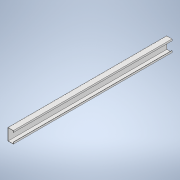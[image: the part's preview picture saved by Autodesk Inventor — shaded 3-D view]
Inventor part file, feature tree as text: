
AUTODESK INVENTOR PART (.ipt)
format: ipt  version: 2020 (Build 240168000, 168)  size: 112,640 bytes
history: native  units: mm
features: extrude x1, sketch x1
ambient origin geometry x8: Origin, YZ Plane, XZ Plane, XY Plane, X Axis, Y Axis, Z Axis, Center Point
bodies: Solid1 (feature_tree)
feature tree (2):
  extrude  "Extrusion1"  Depth=175.0mm
  sketch  "Sketch1"  dims[d0=80.0mm d1=175.0mm d2=25.0mm d3=25.0mm d4=3.5mm d5=2355.0mm d6=0.0mm]
